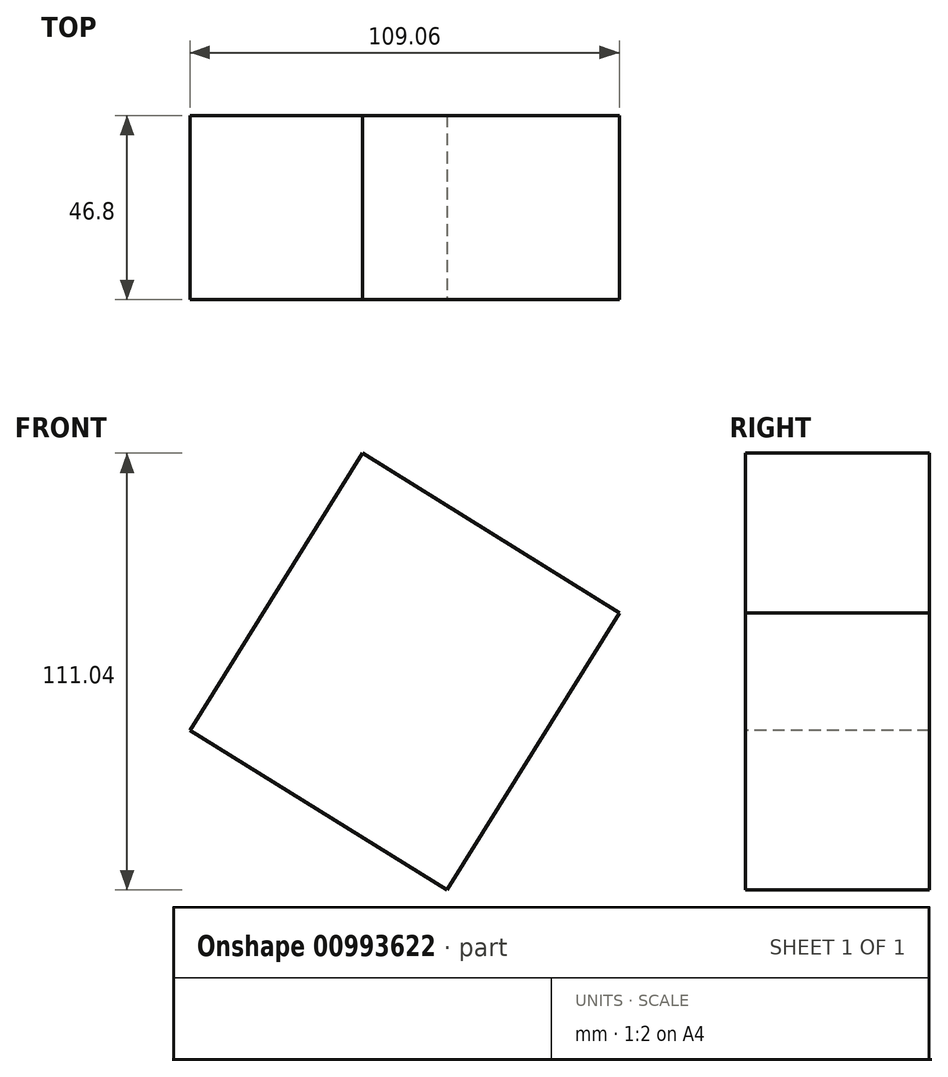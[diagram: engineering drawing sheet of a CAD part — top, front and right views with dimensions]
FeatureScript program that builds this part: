
annotation { "Feature Type Name" : "Feature", "Feature Type Description" : "" }
export const myFeature = defineFeature(function(context is Context, id is Id, definition is map)
    precondition{}
    {
        {
            var Q0;
            Q0=qCreatedBy(makeId("Front.planeOp"),FACE);
            var sketch = newSketch(context, id + "F0", { "sketchPlane" : qUnion([Q0])});
            skLineSegment(sketch, "E0", {"start": v(-31.29, 0) * mm, "end": v(-31.29, -35.37) * mm});
            skLineSegment(sketch, "E1", {"start": v(-31.29, -35.37) * mm, "end": v(41.12, 0) * mm});
            skLineSegment(sketch, "E2", {"start": v(41.12, 0) * mm, "end": v(-24.13, 40.56) * mm});
            skLineSegment(sketch, "E3", {"start": v(-24.13, 40.56) * mm, "end": v(-49.34, 0) * mm});
            skLineSegment(sketch, "E4", {"start": v(-49.34, 0) * mm, "end": v(-31.29, 0) * mm});
            skSolve(sketch);
        }
        {
            var Q0;
            Q0=sQuery(id+"F0.wireOp",EDGE,"E0");
            var Q1;
            Q1=sQuery(id+"F0.wireOp",EDGE,"E1");
            var Q2;
            Q2=sQuery(id+"F0.wireOp",EDGE,"E2");
            var Q3;
            Q3=sQuery(id+"F0.wireOp",EDGE,"E4");
            var Q4;
            Q4=sQuery(id+"F0.wireOp",EDGE,"E3");
            extrude(context, id + "F1", {"bodyType" : ToolBodyType.SURFACE, "surfaceEntities" : qUnion([Q0, Q1, Q2, Q3, Q4]), "depth" : 46.8 * mm, "offsetDistance" : 25.4 * mm});
        }
        {
            var Q0;
            Q0=makeQuery(id+"F1.opExtrude","SWEPT_FACE",FACE,{"disambiguationData":[OSD([sQuery(id+"F0.wireOp",EDGE,"E2")])]});
            extrude(context, id + "F2", {"entities" : qUnion([Q0]), "depth" : 82.99 * mm, "offsetDistance" : 25.4 * mm});
        }
    });
